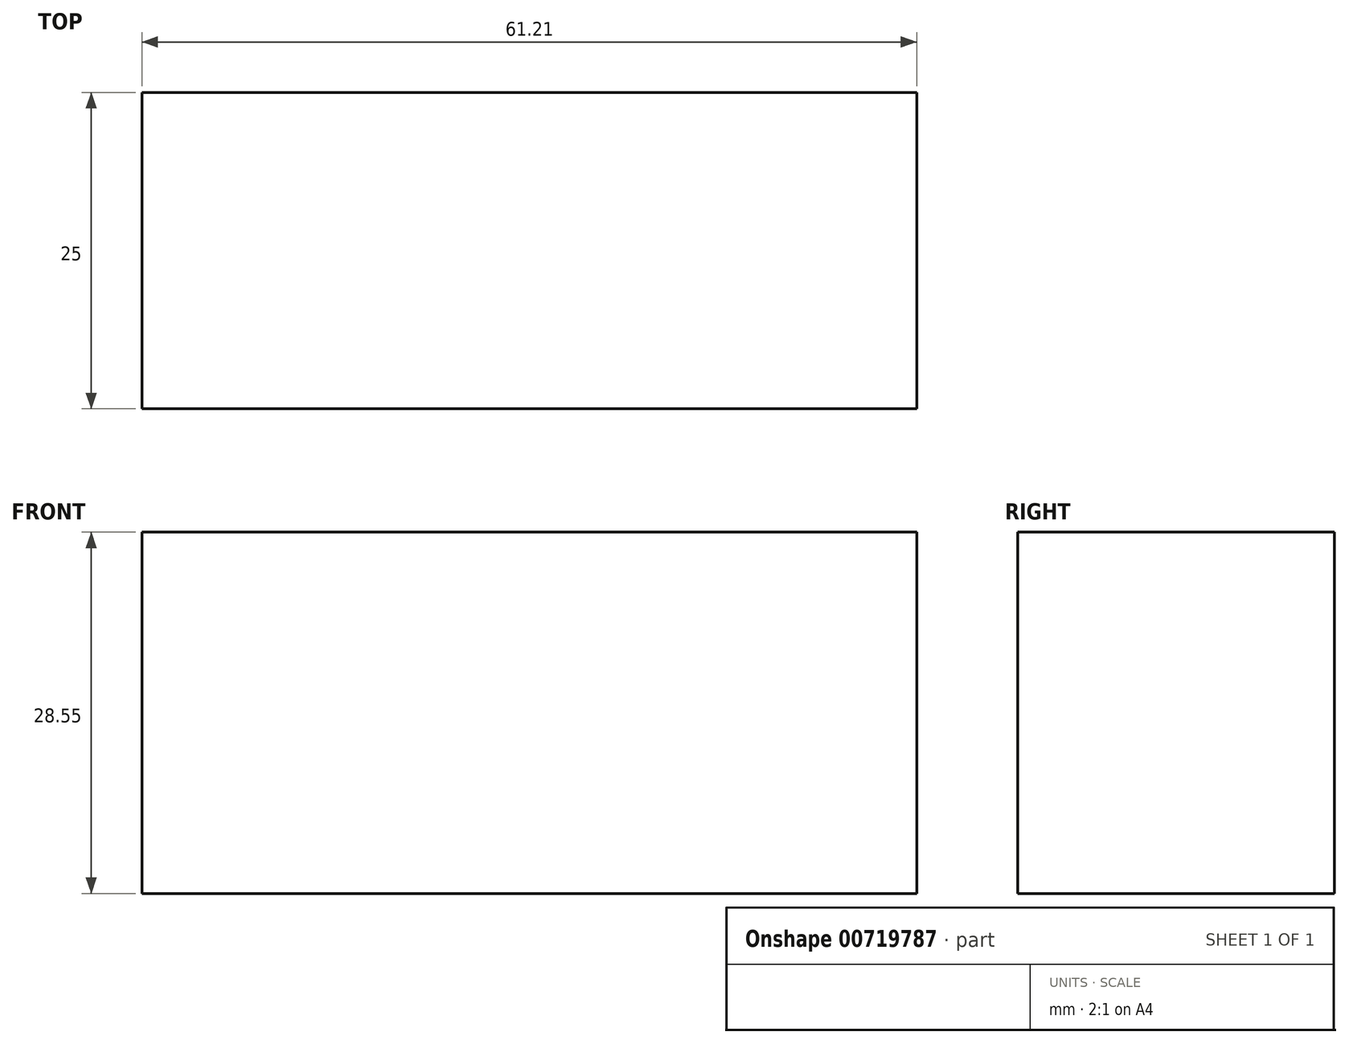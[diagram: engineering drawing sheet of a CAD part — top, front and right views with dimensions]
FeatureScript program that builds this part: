
annotation { "Feature Type Name" : "Feature", "Feature Type Description" : "" }
export const myFeature = defineFeature(function(context is Context, id is Id, definition is map)
    precondition{}
    {
        {
            var Q0;
            Q0=qCreatedBy(makeId("Front.planeOp"),FACE);
            var sketch = newSketch(context, id + "F0", { "sketchPlane" : qUnion([Q0])});
            skLineSegment(sketch, "E0.bottom", {"start": v(-92.84, 43.76) * mm, "end": v(-87.24, 43.76) * mm});
            skLineSegment(sketch, "E0.top", {"start": v(-92.84, 38.35) * mm, "end": v(-87.24, 38.35) * mm});
            skLineSegment(sketch, "E0.left", {"start": v(-92.84, 43.76) * mm, "end": v(-92.84, 38.35) * mm});
            skLineSegment(sketch, "E0.right", {"start": v(-87.24, 43.76) * mm, "end": v(-87.24, 38.35) * mm});
            skLineSegment(sketch, "E1.bottom", {"start": v(-40.59, 8.12) * mm, "end": v(-101.8, 8.12) * mm});
            skLineSegment(sketch, "E1.top", {"start": v(-40.59, -20.43) * mm, "end": v(-101.8, -20.43) * mm});
            skLineSegment(sketch, "E1.left", {"start": v(-40.59, 8.12) * mm, "end": v(-40.59, -20.43) * mm});
            skLineSegment(sketch, "E1.right", {"start": v(-101.8, 8.12) * mm, "end": v(-101.8, -20.43) * mm});
            skSolve(sketch);
        }
        {
            var Q0;
            Q0=makeQuery(id+"F0.imprint","IMPRINT",FACE,{"disambiguationData":[TD([[makeQuery(id+"F0.imprint","IMPRINT",EDGE,{"derivedFrom":sQuery(id+"F0.wireOp",EDGE,"E1.bottom")}),1.0]])]});
            extrude(context, id + "F1", {"entities" : qUnion([Q0]), "depth" : 25 * mm, "offsetDistance" : 25 * mm});
        }
    });
